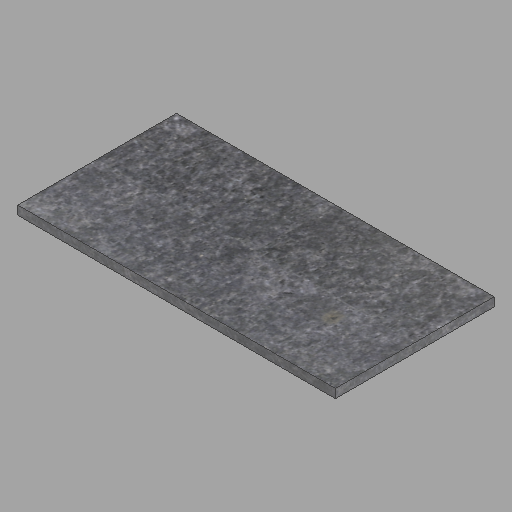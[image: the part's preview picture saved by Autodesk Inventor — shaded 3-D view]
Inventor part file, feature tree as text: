
AUTODESK INVENTOR PART (.ipt)
format: ipt  version: 2023 (Build 270158000, 158)  size: 222,720 bytes
history: native  units: in
note: dims shown in document units (in); Inventor stores cm internally (conversion verified against a paired STEP export)
features: other x1, extrude x1, sketch x1
ambient origin geometry x8: Origin, YZ Plane, XZ Plane, XY Plane, X Axis, Y Axis, Z Axis, Center Point
bodies: Solid1 (feature_tree)
feature tree (3):
  other  "18x36x2-67"
  extrude  "Extrusion1"  Depth=18.0in
  sketch  "Sketch1"  dims[d0=36.0in d1=18.0in d2=1.0in d3=0.0in]
